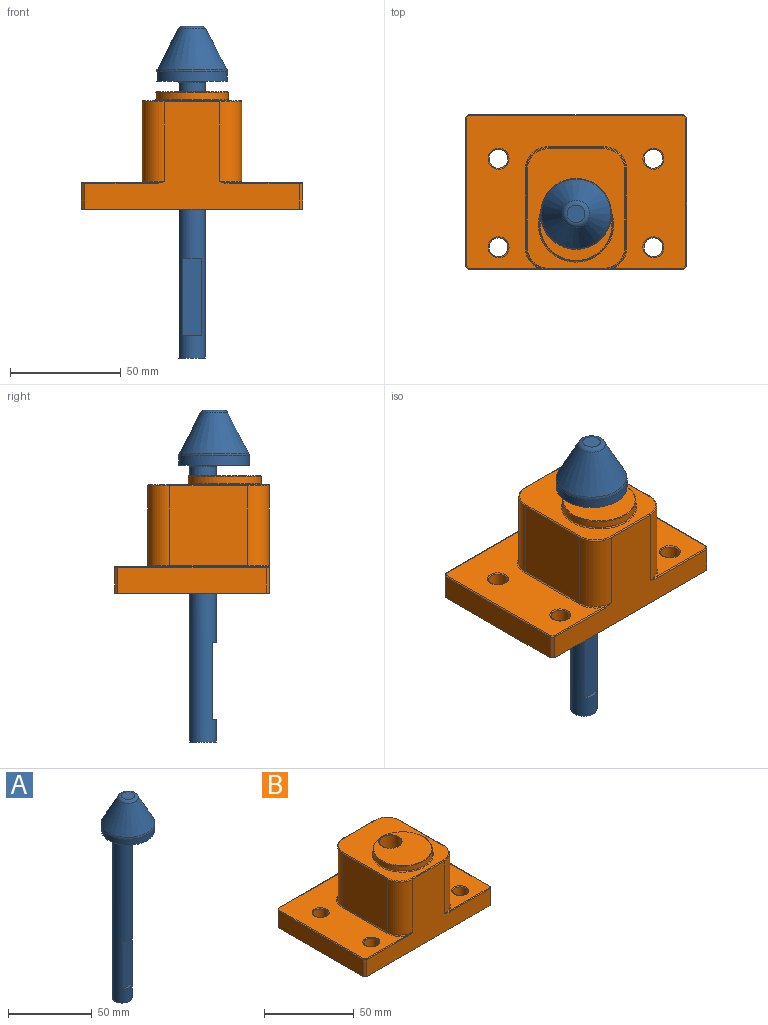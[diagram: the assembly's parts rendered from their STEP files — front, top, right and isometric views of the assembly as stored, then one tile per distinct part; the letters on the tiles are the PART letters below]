
ASSEMBLY  parts=2 mates=1
PART A: 12 faces, bbox 34.6x34.6x150 mm
  f0: cylinder r=6mm len=124.5mm, axis (0,0,1), area 4379.6mm2, adj f7,f8,f9,f10,f11
  f1: plane 7.98x7.98mm, normal (0,0,1), area 50mm2, adj f6
  f2: plane 32x32mm, normal (0,0,-1), area 671.5mm2, adj f3,f8
  f3: cylinder r=16mm len=32mm, axis (0,0,1), area 440.7mm2, adj f2,f5
  f4: cone r=16mm half-angle=27.7deg, axis (0,0,-1), area 1408.8mm2, adj f5,f6
  f5: torus R=13.5mm, axis (0,0,-1), area 120.8mm2, adj f3,f4
  f6: torus R=3.99mm, axis (0,0,-1), area 89.1mm2, adj f1,f4
  f7: plane 12x12mm, normal (0,0,-1), area 113.1mm2, adj f0
  f8: cone r=6mm half-angle=45deg, axis (0,0,1), area 27.8mm2, adj f0,f2
  f9: plane 8.16x1.6mm, normal (0,0,-1), area 9mm2, adj f0,f11
  f10: plane 8.16x1.6mm, normal (0,0,1), area 9mm2, adj f0,f11
  f11: plane 35x8.16mm, normal (0,-1,0), area 285.5mm2, adj f0,f9,f10
PART B: 58 faces, bbox 100x71.7x53 mm
  f0: plane 99x69mm, normal (0,0,1), area 4094.2mm2, adj f25,f26,f27,f28,f29,f30,f32,f33
  f1: plane 67x11.5mm, normal (-1,0,0), area 770.5mm2, adj f9,f23,f24,f37
  f2: plane 97x48.5mm, normal (0,-1,0), area 2043.9mm2, adj f9,f17,f18,f22,f23,f31,f33,f34
  f3: plane 67x11.5mm, normal (1,0,0), area 770.5mm2, adj f9,f21,f22,f40
  f4: cylinder r=4.25mm len=11.5mm, axis (0,0,-1), area 307.1mm2, adj f9,f52
  f5: cylinder r=4.25mm len=11.5mm, axis (0,0,-1), area 307.1mm2, adj f9,f53
  f6: cylinder r=4.25mm len=11.5mm, axis (0,0,-1), area 307.1mm2, adj f9,f54
  f7: plane 97x11.5mm, normal (0,1,0), area 1115.5mm2, adj f9,f21,f24,f41
  f8: cylinder r=4.25mm len=11.5mm, axis (0,0,-1), area 307.1mm2, adj f9,f55
  f9: plane 100x70mm, normal (0,0,-1), area 6645.8mm2, adj f1,f2,f3,f4,f5,f6,f7,f8
  f10: plane 36x35mm, normal (-1,0,0), area 1260mm2, adj f17,f20,f27,f48
  f11: plane 36x35mm, normal (1,0,0), area 1260mm2, adj f18,f19,f30,f45
  f12: plane 36x25mm, normal (0,1,0), area 900mm2, adj f19,f20,f26,f44
  f13: plane 54x44mm, normal (0,0,1), area 1390.6mm2, adj f43,f44,f45,f46,f47,f48,f49,f50
  f14: cylinder r=6.25mm len=52.75mm, axis (0,0,-1), area 2071.5mm2, adj f9,f57
  f15: cylinder r=16.5mm len=33mm, axis (0,0,-1), area 336.9mm2, adj f51,f56
  f16: plane 32.5x32.5mm, normal (0,0,1), area 696.8mm2, adj f56,f57
  f17: cylinder r=10mm len=36mm, axis (0,0,1), area 565.5mm2, adj f2,f10,f29,f50
  f18: cylinder r=10mm len=36mm, axis (0,0,-1), area 565.5mm2, adj f2,f11,f32,f47
  f19: cylinder r=10mm len=36mm, axis (0,0,1), area 565.5mm2, adj f11,f12,f28,f43
  f20: cylinder r=10mm len=36mm, axis (0,0,-1), area 565.5mm2, adj f10,f12,f25,f46
  f21: plane 11.5x1.5mm, normal (0.71,0.71,0), area 24.4mm2, adj f3,f7,f9,f42
  f22: plane 11.5x1.5mm, normal (0.71,-0.71,0), area 24.4mm2, adj f2,f3,f9,f38
  f23: plane 11.5x1.5mm, normal (-0.71,-0.71,0), area 24.4mm2, adj f1,f2,f9,f35
  f24: plane 11.5x1.5mm, normal (-0.71,0.71,0), area 24.4mm2, adj f1,f7,f9,f39
  f25: torus R=10.5mm, axis (0,0,1), area 12.6mm2, adj f0,f20,f26,f27
  f26: cylinder r=0.5mm len=25mm, axis (-1,0,0), area 19.6mm2, adj f0,f12,f25,f28
  f27: cylinder r=0.5mm len=35mm, axis (0,-1,0), area 27.5mm2, adj f0,f10,f25,f29
  f28: torus R=10.5mm, axis (0,0,1), area 12.6mm2, adj f0,f19,f26,f30
  f29: torus R=10.5mm, axis (0,0,1), area 10.8mm2, adj f0,f17,f27,f31
  f30: cylinder r=0.5mm len=35mm, axis (0,1,0), area 27.5mm2, adj f0,f11,f28,f32
  f31: bspline ~4.47x1mm, area 1.7mm2, adj f2,f29,f33
  f32: torus R=10.5mm, axis (0,0,1), area 10.8mm2, adj f0,f18,f30,f34
  f33: cylinder r=0.5mm len=31.53mm, axis (-1,0,0), area 24.7mm2, adj f0,f2,f31,f35
  f34: bspline ~4.47x1mm, area 1.7mm2, adj f2,f32,f36
  f35: cylinder r=0.5mm len=1.85mm, axis (0.71,-0.71,0), area 1.5mm2, adj f0,f23,f33,f37
  f36: cylinder r=0.5mm len=31.53mm, axis (-1,0,0), area 24.7mm2, adj f0,f2,f34,f38
  f37: cylinder r=0.5mm len=67mm, axis (0,1,0), area 52.5mm2, adj f0,f1,f35,f39
  f38: cylinder r=0.5mm len=1.85mm, axis (-0.71,-0.71,0), area 1.5mm2, adj f0,f22,f36,f40
  f39: cylinder r=0.5mm len=1.85mm, axis (0.71,0.71,0), area 1.5mm2, adj f0,f24,f37,f41
  f40: cylinder r=0.5mm len=67mm, axis (0,-1,0), area 52.5mm2, adj f0,f3,f38,f42
  f41: cylinder r=0.5mm len=97mm, axis (1,0,0), area 76mm2, adj f0,f7,f39,f42
  f42: cylinder r=0.5mm len=1.85mm, axis (-0.71,0.71,0), area 1.5mm2, adj f0,f21,f40,f41
  f43: torus R=9.5mm, axis (0,0,1), area 12.1mm2, adj f13,f19,f44,f45
  f44: cylinder r=0.5mm len=25mm, axis (1,0,0), area 19.6mm2, adj f12,f13,f43,f46
  f45: cylinder r=0.5mm len=35mm, axis (0,-1,0), area 27.5mm2, adj f11,f13,f43,f47
  f46: torus R=9.5mm, axis (0,0,1), area 12.1mm2, adj f13,f20,f44,f48
  f47: torus R=9.5mm, axis (0,0,1), area 12.1mm2, adj f13,f18,f45,f49
  f48: cylinder r=0.5mm len=35mm, axis (0,1,0), area 27.5mm2, adj f10,f13,f46,f50
  f49: cylinder r=0.5mm len=25mm, axis (-1,0,0), area 19.6mm2, adj f2,f13,f47,f50
  f50: torus R=9.5mm, axis (0,0,1), area 12.1mm2, adj f13,f17,f48,f49
  f51: torus R=17mm, axis (0,0,1), area 82.3mm2, adj f13,f15
  f52: torus R=4.75mm, axis (0,0,1), area 21.9mm2, adj f0,f4
  f53: torus R=4.75mm, axis (0,0,1), area 21.9mm2, adj f0,f5
  f54: torus R=4.75mm, axis (0,0,1), area 21.9mm2, adj f0,f6
  f55: torus R=4.75mm, axis (0,0,1), area 21.9mm2, adj f0,f8
  f56: cone r=16.25mm half-angle=45deg, axis (0,0,-1), area 36.4mm2, adj f15,f16
  f57: cone r=6.25mm half-angle=45deg, axis (0,0,1), area 14.2mm2, adj f14,f16
PLACE A t=(53.31,-2.37,13.29)mm
PLACE B t=(3.31,-27.37,-44.46)mm
MATE slider A.f0 <-> B.f14  axis (0,0,1) through (53.31,2.63,-49.46)mm
